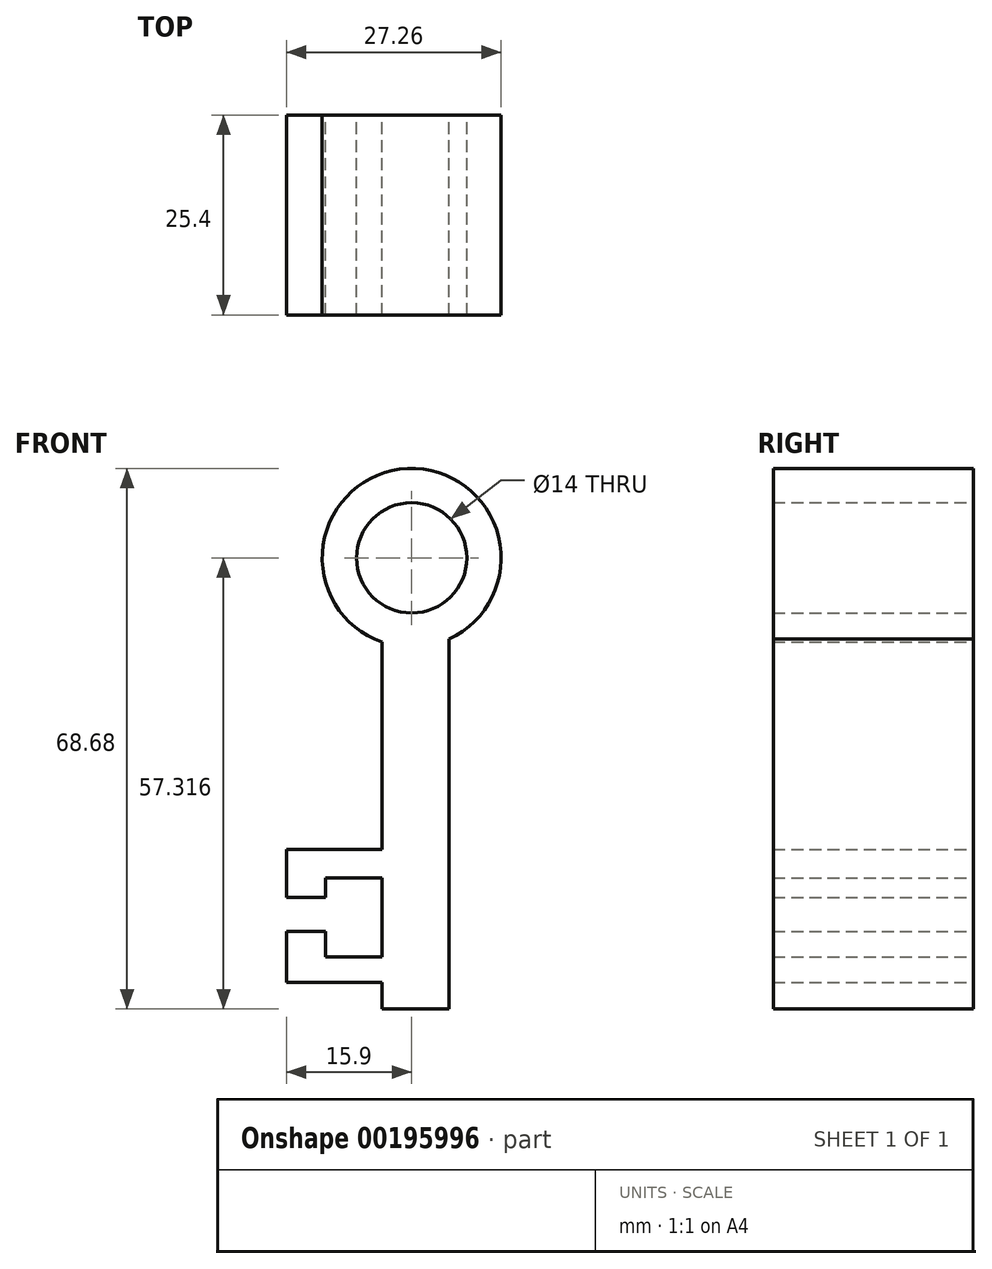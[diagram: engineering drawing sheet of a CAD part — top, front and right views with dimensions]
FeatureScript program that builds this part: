
annotation { "Feature Type Name" : "Feature", "Feature Type Description" : "" }
export const myFeature = defineFeature(function(context is Context, id is Id, definition is map)
    precondition{}
    {
        {
            var Q0;
            Q0=qCreatedBy(makeId("Front.planeOp"),FACE);
            var sketch = newSketch(context, id + "F0", { "sketchPlane" : qUnion([Q0])});
            skCircle(sketch, "E0", {"center": v(0, 37.04) * mm, "radius": 11.36 * mm});
            skCircle(sketch, "E1", {"center": v(0, 37.04) * mm, "radius": 7 * mm});
            skLineSegment(sketch, "E2", {"start": v(-3.78, 26.32) * mm, "end": v(-3.78, -20.28) * mm});
            skLineSegment(sketch, "E3", {"start": v(-3.78, -20.28) * mm, "end": v(4.75, -20.28) * mm});
            skLineSegment(sketch, "E4", {"start": v(4.75, -20.28) * mm, "end": v(4.75, 26.72) * mm});
            skLineSegment(sketch, "E5", {"start": v(-3.78, 0) * mm, "end": v(-15.9, 0) * mm});
            skLineSegment(sketch, "E6", {"start": v(-15.9, 0) * mm, "end": v(-15.9, -6.1) * mm});
            skLineSegment(sketch, "E7", {"start": v(-15.9, -6.1) * mm, "end": v(-10.97, -6.1) * mm});
            skLineSegment(sketch, "E8", {"start": v(-10.97, -6.1) * mm, "end": v(-10.97, -3.63) * mm});
            skLineSegment(sketch, "E9", {"start": v(-10.97, -3.63) * mm, "end": v(-3.78, -3.63) * mm});
            skLineSegment(sketch, "E10", {"start": v(-15.9, -10.41) * mm, "end": v(-10.97, -10.41) * mm});
            skLineSegment(sketch, "E11", {"start": v(-15.9, -10.41) * mm, "end": v(-15.9, -16.92) * mm});
            skLineSegment(sketch, "E12", {"start": v(-15.9, -16.92) * mm, "end": v(-3.78, -16.92) * mm});
            skLineSegment(sketch, "E13", {"start": v(-10.97, -10.41) * mm, "end": v(-10.97, -13.67) * mm});
            skPoint(sketch, "E13.endSnap0", {"position": v(-15.9, -13.67) * mm});
            skLineSegment(sketch, "E14", {"start": v(-10.97, -13.67) * mm, "end": v(-3.78, -13.67) * mm});
            skSolve(sketch);
        }
        {
            var Q0;
            Q0 = qSketchRegion(id + "F0", true);
            extrude(context, id + "F1", {"entities" : qUnion([Q0]), "depth" : 25.4 * mm});
        }
    });
